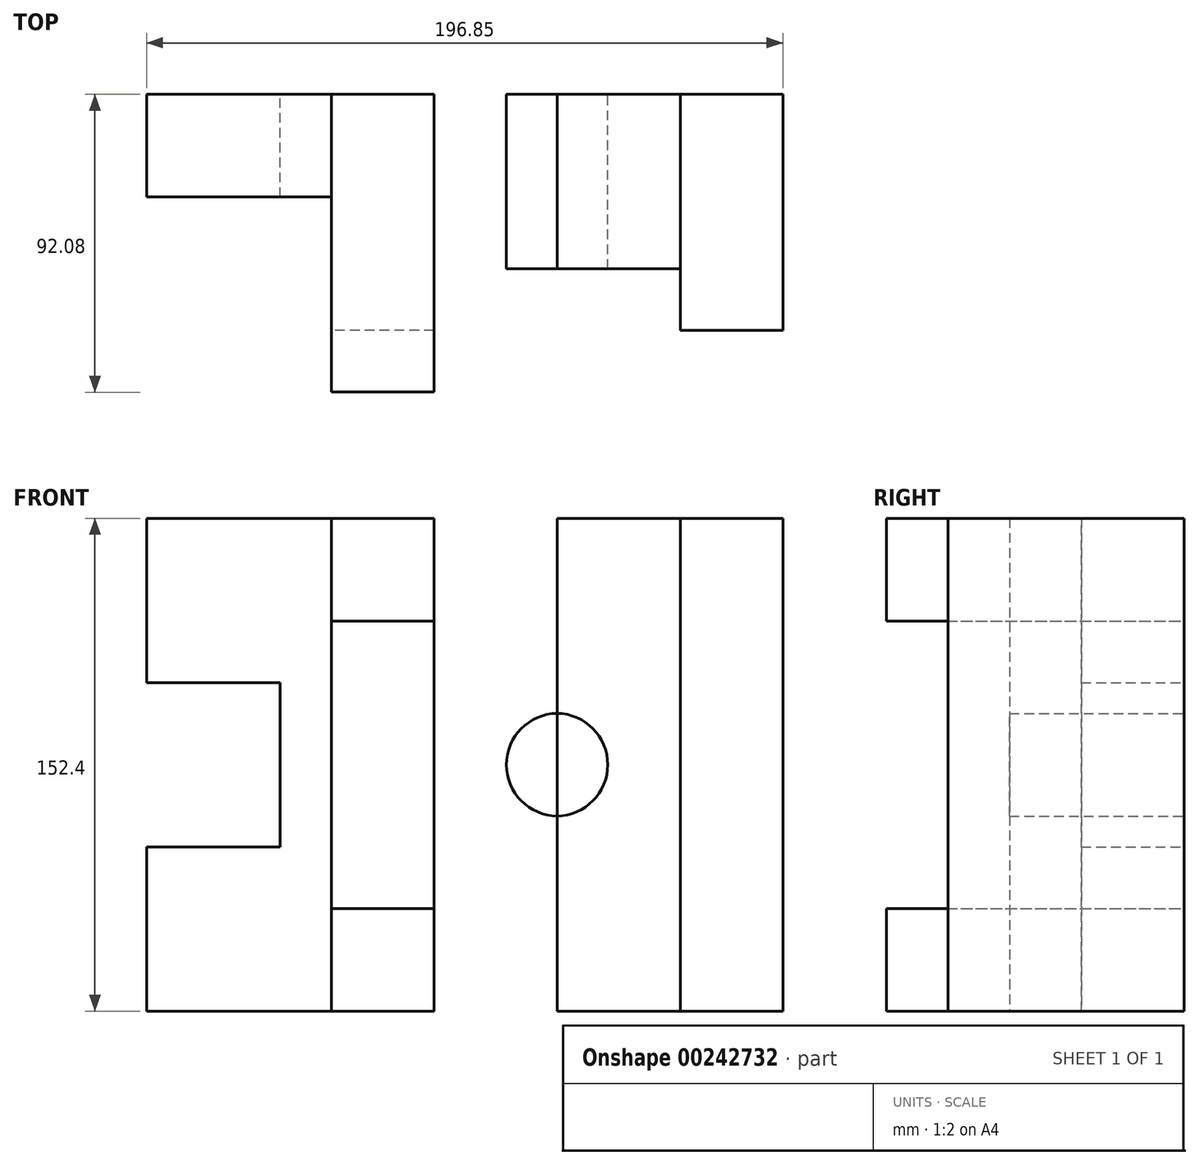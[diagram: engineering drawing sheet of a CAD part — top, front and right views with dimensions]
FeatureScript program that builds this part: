
annotation { "Feature Type Name" : "Feature", "Feature Type Description" : "" }
export const myFeature = defineFeature(function(context is Context, id is Id, definition is map)
    precondition{}
    {
        {
            var Q0;
            Q0=qCreatedBy(makeId("Front.planeOp"),FACE);
            var sketch = newSketch(context, id + "F0", { "sketchPlane" : qUnion([Q0])});
            skLineSegment(sketch, "E0.bottom", {"start": v(127.2, 76.2) * mm, "end": v(-126.8, 76.2) * mm});
            skLineSegment(sketch, "E0.top", {"start": v(127.2, -76.2) * mm, "end": v(-126.8, -76.2) * mm});
            skLineSegment(sketch, "E0.left", {"start": v(127.2, 76.2) * mm, "end": v(127.2, -76.2) * mm});
            skLineSegment(sketch, "E0.right", {"start": v(-126.8, 76.2) * mm, "end": v(-126.8, -76.2) * mm});
            skPoint(sketch, "E0.middle", {"position": v(0.2, 0) * mm});
            skLineSegment(sketch, "E1.bottom", {"start": v(127.2, -76.2) * mm, "end": v(70.06, -76.2) * mm});
            skLineSegment(sketch, "E1.top", {"start": v(127.2, -76.2) * mm, "end": v(70.06, -76.2) * mm});
            skLineSegment(sketch, "E1.left", {"start": v(127.2, -76.2) * mm, "end": v(127.2, -76.2) * mm});
            skLineSegment(sketch, "E1.right", {"start": v(70.06, -76.2) * mm, "end": v(70.06, -76.2) * mm});
            skLineSegment(sketch, "E2.bottom", {"start": v(70.06, -76.2) * mm, "end": v(127.2, -76.2) * mm});
            skLineSegment(sketch, "E2.top", {"start": v(70.06, 76.2) * mm, "end": v(127.2, 76.2) * mm});
            skLineSegment(sketch, "E2.left", {"start": v(70.06, -76.2) * mm, "end": v(70.06, 76.2) * mm});
            skLineSegment(sketch, "E2.right", {"start": v(127.2, -76.2) * mm, "end": v(127.2, 76.2) * mm});
            skLineSegment(sketch, "E3", {"start": v(127.2, -76.2) * mm, "end": v(127.2, -25.4) * mm});
            skLineSegment(sketch, "E4", {"start": v(127.2, -25.4) * mm, "end": v(127.2, 25.4) * mm});
            skLineSegment(sketch, "E5.bottom", {"start": v(127.2, 25.4) * mm, "end": v(85.93, 25.4) * mm});
            skLineSegment(sketch, "E5.top", {"start": v(127.2, -25.4) * mm, "end": v(85.93, -25.4) * mm});
            skLineSegment(sketch, "E5.left", {"start": v(127.2, 25.4) * mm, "end": v(127.2, -25.4) * mm});
            skLineSegment(sketch, "E5.right", {"start": v(85.93, 25.4) * mm, "end": v(85.93, -25.4) * mm});
            skLineSegment(sketch, "E6", {"start": v(70.06, 76.2) * mm, "end": v(38.3, 76.2) * mm});
            skLineSegment(sketch, "E7", {"start": v(38.3, 76.2) * mm, "end": v(38.3, -76.2) * mm});
            skLineSegment(sketch, "E8", {"start": v(38.3, 76.2) * mm, "end": v(38.3, 44.45) * mm});
            skLineSegment(sketch, "E9.top", {"start": v(70.06, 44.45) * mm, "end": v(38.3, 44.45) * mm});
            skLineSegment(sketch, "E9.left", {"start": v(70.06, 76.2) * mm, "end": v(70.06, 44.45) * mm});
            skArc(sketch, "E10", {"start": v(0.2, -15.87) * mm, "mid": v(15.88, 0) * mm, "end": v(0.2, 15.87) * mm});
            skLineSegment(sketch, "E11", {"start": v(0.2, 76.2) * mm, "end": v(0.2, -76.2) * mm});
            skLineSegment(sketch, "E12", {"start": v(70.06, -76.2) * mm, "end": v(70.06, -44.45) * mm});
            skLineSegment(sketch, "E13", {"start": v(38.3, -44.45) * mm, "end": v(70.06, -44.45) * mm});
            skLineSegment(sketch, "E14.bottom", {"start": v(70.06, -76.2) * mm, "end": v(38.3, -76.2) * mm});
            skLineSegment(sketch, "E14.top", {"start": v(70.06, -44.45) * mm, "end": v(38.3, -44.45) * mm});
            skLineSegment(sketch, "E14.right", {"start": v(38.3, -76.2) * mm, "end": v(38.3, -44.45) * mm});
            skLineSegment(sketch, "E15.MirrorCS", {"start": v(-37.9, 76.2) * mm, "end": v(-37.9, -76.2) * mm});
            skLineSegment(sketch, "E16.MirrorCS", {"start": v(-69.64, 44.45) * mm, "end": v(-37.9, 44.45) * mm});
            skLineSegment(sketch, "E17.MirrorCS", {"start": v(-69.64, -76.2) * mm, "end": v(-69.64, 76.2) * mm});
            skLineSegment(sketch, "E18.MirrorCS", {"start": v(-69.64, 76.2) * mm, "end": v(-37.9, 76.2) * mm});
            skLineSegment(sketch, "E19.MirrorCS", {"start": v(-37.9, -44.45) * mm, "end": v(-69.64, -44.45) * mm});
            skLineSegment(sketch, "E20.MirrorCS", {"start": v(-69.64, -76.2) * mm, "end": v(-37.9, -76.2) * mm});
            skLineSegment(sketch, "E21.MirrorCS", {"start": v(-126.8, -25.4) * mm, "end": v(-85.52, -25.4) * mm});
            skLineSegment(sketch, "E22.MirrorCS", {"start": v(-85.52, 25.4) * mm, "end": v(-85.52, -25.4) * mm});
            skLineSegment(sketch, "E23.MirrorCS", {"start": v(-126.8, 25.4) * mm, "end": v(-85.52, 25.4) * mm});
            skLineSegment(sketch, "E24.MirrorCS", {"start": v(-126.8, -76.2) * mm, "end": v(-126.8, 76.2) * mm});
            skLineSegment(sketch, "E25.MirrorCS", {"start": v(-69.64, -76.2) * mm, "end": v(-126.8, -76.2) * mm});
            skArc(sketch, "E26.MirrorCS", {"start": v(0.2, -15.87) * mm, "mid": v(-15.46, 0) * mm, "end": v(0.2, 15.87) * mm});
            skSolve(sketch);
        }
        {
            var Q0;
            {var subQ9=sQuery(id+"F0.wireOp",EDGE,"E21.MirrorCS");Q0=makeQuery(id+"F0.imprint","IMPRINT",FACE,{"disambiguationData":[TD([[makeQuery(id+"F0.imprint","IMPRINT",EDGE,{"derivedFrom":subQ9}),-1.0]])]});}
            var Q1;
            Q1=makeQuery(id+"F0.imprint","IMPRINT",FACE,{"disambiguationData":[TD([[makeQuery(id+"F0.imprint","IMPRINT",EDGE,{"derivedFrom":sQuery(id+"F0.wireOp",EDGE,"E2.bottom")}),1.0]])]});
            extrude(context, id + "F1", {"entities" : qUnion([Q0, Q1]), "depth" : 31.75 * mm});
        }
        {
            var Q0;
            Q0=makeQuery(id+"F0.imprint","IMPRINT",FACE,{"disambiguationData":[TD([[makeQuery(id+"F0.imprint","IMPRINT",EDGE,{"derivedFrom":sQuery(id+"F0.wireOp",EDGE,"E7")}),-1.0]])]});
            var Q1;
            {var subQ0=sQuery(id+"F0.wireOp",EDGE,"E26.MirrorCS");Q1=makeQuery(id+"F0.imprint","IMPRINT",FACE,{"disambiguationData":[TD([[makeQuery(id+"F0.imprint","IMPRINT",EDGE,{"derivedFrom":subQ0}),1.0]])]});}
            extrude(context, id + "F2", {"entities" : qUnion([Q0, Q1]), "depth" : 53.97 * mm});
        }
        {
            var Q0;
            Q0=makeQuery(id+"F0.imprint","IMPRINT",FACE,{"disambiguationData":[TD([[makeQuery(id+"F0.imprint","IMPRINT",EDGE,{"derivedFrom":sQuery(id+"F0.wireOp",EDGE,"E2.left")}),1.0]])]});
            var Q1;
            {var subQ0=sQuery(id+"F0.wireOp",EDGE,"E16.MirrorCS");Q1=makeQuery(id+"F0.imprint","IMPRINT",FACE,{"disambiguationData":[TD([[makeQuery(id+"F0.imprint","IMPRINT",EDGE,{"derivedFrom":subQ0}),-1.0]])]});}
            extrude(context, id + "F3", {"entities" : qUnion([Q0, Q1]), "depth" : 73.02 * mm});
        }
        {
            var Q0;
            {var subQ3=sQuery(id+"F0.wireOp",EDGE,"E16.MirrorCS");Q0=makeQuery(id+"F0.imprint","IMPRINT",FACE,{"disambiguationData":[TD([[makeQuery(id+"F0.imprint","IMPRINT",EDGE,{"derivedFrom":subQ3}),1.0]])]});}
            var Q1;
            Q1=makeQuery(id+"F0.imprint","IMPRINT",FACE,{"disambiguationData":[TD([[makeQuery(id+"F0.imprint","IMPRINT",EDGE,{"derivedFrom":sQuery(id+"F0.wireOp",EDGE,"E6")}),1.0]])]});
            var Q2;
            Q2=makeQuery(id+"F0.imprint","IMPRINT",FACE,{"disambiguationData":[TD([[makeQuery(id+"F0.imprint","IMPRINT",EDGE,{"derivedFrom":sQuery(id+"F0.wireOp",EDGE,"E14.bottom")}),-1.0]])]});
            var Q3;
            {var subQ2=sQuery(id+"F0.wireOp",EDGE,"E19.MirrorCS");Q3=makeQuery(id+"F0.imprint","IMPRINT",FACE,{"disambiguationData":[TD([[makeQuery(id+"F0.imprint","IMPRINT",EDGE,{"derivedFrom":subQ2}),1.0]])]});}
            extrude(context, id + "F4", {"entities" : qUnion([Q0, Q1, Q2, Q3]), "depth" : 92.07 * mm});
        }
    });
